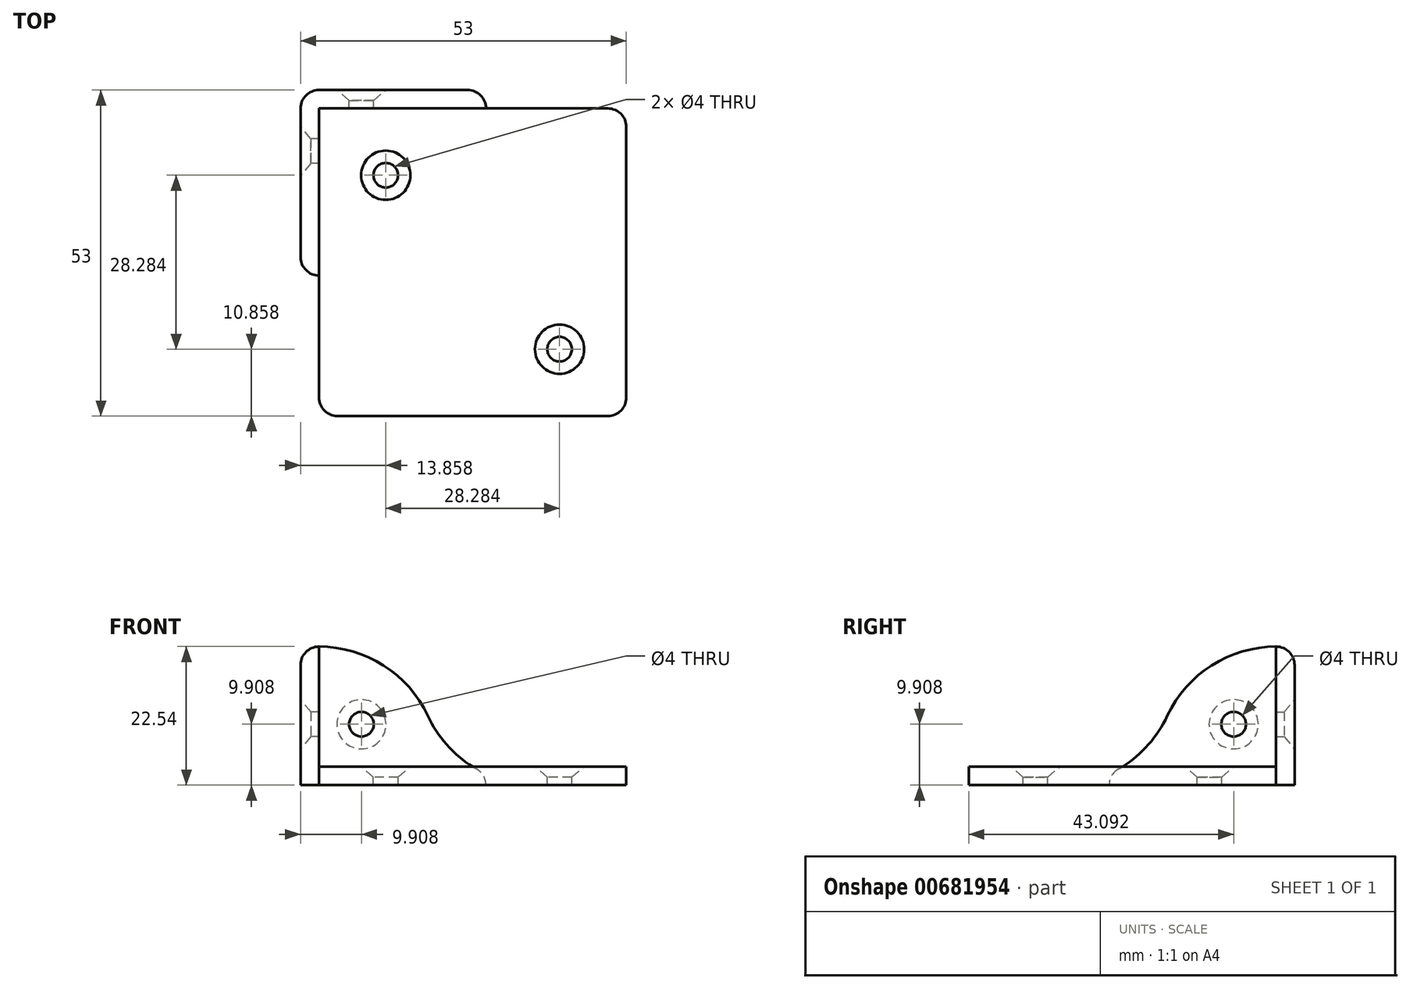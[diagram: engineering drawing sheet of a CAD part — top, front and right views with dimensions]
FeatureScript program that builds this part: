
annotation { "Feature Type Name" : "Feature", "Feature Type Description" : "" }
export const myFeature = defineFeature(function(context is Context, id is Id, definition is map)
    precondition{}
    {
        {
            var Q0;
            Q0=qCreatedBy(makeId("Top.planeOp"),FACE);
            var sketch = newSketch(context, id + "F0", { "sketchPlane" : qUnion([Q0])});
            skLineSegment(sketch, "E0.bottom", {"start": v(-25, 25) * mm, "end": v(25, 25) * mm});
            skLineSegment(sketch, "E0.top", {"start": v(-25, -25) * mm, "end": v(25, -25) * mm});
            skLineSegment(sketch, "E0.left", {"start": v(-25, 22) * mm, "end": v(-25, -25) * mm});
            skLineSegment(sketch, "E0.right", {"start": v(25, 25) * mm, "end": v(25, -25) * mm});
            skPoint(sketch, "E0.middle", {"position": v(0, 0) * mm});
            skLineSegment(sketch, "E1", {"start": v(-25, 25) * mm, "end": v(25, -25) * mm, "construction": true});
            skCircle(sketch, "E2", {"center": v(-14.14, 14.14) * mm, "radius": 2 * mm, "construction": true});
            skCircle(sketch, "E3", {"center": v(14.14, -14.14) * mm, "radius": 2 * mm, "construction": true});
            skCircle(sketch, "E4", {"center": v(-14.14, 14.14) * mm, "radius": 4 * mm, "construction": true});
            skCircle(sketch, "E5", {"center": v(14.14, -14.14) * mm, "radius": 4 * mm, "construction": true});
            skLineSegment(sketch, "E6.left", {"start": v(-28, 28) * mm, "end": v(-28, 25) * mm});
            skLineSegment(sketch, "E7", {"start": v(-28, 25) * mm, "end": v(-25, 22) * mm});
            skLineSegment(sketch, "E8", {"start": v(-28, 28) * mm, "end": v(-25, 25) * mm});
            skSolve(sketch);
        }
        {
            var Q0;
            Q0=makeQuery(id+"F0.imprint","IMPRINT",FACE,{"disambiguationData":[TD([[makeQuery(id+"F0.imprint","IMPRINT",EDGE,{"derivedFrom":sQuery(id+"F0.wireOp",EDGE,"E0.bottom")}),-1.0]])]});
            var Q1;
            Q1=makeQuery(id+"F0.imprint","IMPRINT",FACE,{"disambiguationData":[TD([[makeQuery(id+"F0.imprint","IMPRINT",EDGE,{"derivedFrom":sQuery(id+"F0.wireOp",EDGE,"E6.bottom")}),-1.0]])]});
            extrude(context, id + "F1", {"entities" : qUnion([Q0, Q1]), "oppositeDirection" : true, "depth" : 3 * mm, "offsetDistance" : 25 * mm});
        }
        {
            var Q0;
            Q0=makeQuery(id+"F1.opExtrude","SWEPT_FACE",FACE,{"disambiguationData":[OSD([sQuery(id+"F0.wireOp",EDGE,"E6.left")])]});
            var sketch = newSketch(context, id + "F2", { "sketchPlane" : qUnion([Q0])});
            skCircle(sketch, "E9", {"center": v(-18.1, 6.9) * mm, "radius": 4 * mm, "construction": true});
            skCircle(sketch, "E10", {"center": v(-18.1, 6.9) * mm, "radius": 2 * mm, "construction": true});
            skLineSegment(sketch, "E11", {"start": v(-25, 0) * mm, "end": v(-18.1, 6.9) * mm, "construction": true});
            skArc(sketch, "E12", {"start": v(-7.3, 8.27) * mm, "mid": v(-3.99, 3.32) * mm, "end": v(0.66, -0.4) * mm});
            skLineSegment(sketch, "E13", {"start": v(-18.1, 6.9) * mm, "end": v(-11.18, 13.82) * mm, "construction": true});
            skLineSegment(sketch, "E14", {"start": v(-28, 19.54) * mm, "end": v(-28, -3) * mm});
            skLineSegment(sketch, "E15", {"start": v(-28, -3) * mm, "end": v(2.17, -3) * mm});
            skArc(sketch, "E16", {"start": v(-7.3, 8.27) * mm, "mid": v(-14.5, 16.48) * mm, "end": v(-25, 19.54) * mm});
            skArc(sketch, "E17", {"start": v(2.17, -3) * mm, "mid": v(1.76, -1.5) * mm, "end": v(0.66, -0.4) * mm});
            skLineSegment(sketch, "E18", {"start": v(-28, 19.54) * mm, "end": v(-25, 19.54) * mm});
            skSolve(sketch);
        }
        {
            var Q0;
            {var subQ3=sQuery(id+"F2.wireOp",EDGE,"E14");Q0=makeQuery(id+"F2.imprint","IMPRINT",FACE,{"disambiguationData":[TD([[makeQuery(id+"F2.imprint","IMPRINT",EDGE,{"derivedFrom":subQ3}),1.0]])]});}
            var Q1;
            {var subQ3=sQuery(id+"F2.wireOp",EDGE,"E17");Q1=makeQuery(id+"F2.imprint","IMPRINT",FACE,{"disambiguationData":[TD([[makeQuery(id+"F2.imprint","IMPRINT",EDGE,{"derivedFrom":subQ3}),1.0]])]});}
            extrude(context, id + "F3", {"entities" : qUnion([Q0, Q1]), "operationType" : NewBodyOperationType.ADD, "oppositeDirection" : true, "depth" : 3 * mm, "offsetDistance" : 25 * mm});
        }
        {
            var Q0;
            Q0=sQuery(id+"F0.wireOp",VERTEX,"E4.center");
            var Q1;
            Q1=sQuery(id+"F0.wireOp",VERTEX,"E5.center");
            var Q2;
            Q2=makeQuery(id+"F1.opExtrude","SWEPT_BODY",BODY,{"disambiguationData":[OSD([sQuery(id+"F0.wireOp",EDGE,"E0.bottom"),sQuery(id+"F0.wireOp",EDGE,"E0.top"),sQuery(id+"F0.wireOp",EDGE,"E0.left"),sQuery(id+"F0.wireOp",EDGE,"E0.right")])]});
            hole(context, id + "F4", {"style" : HoleStyle.C_SINK, "endStyle" : HoleEndStyle.THROUGH, "holeDiameter" : 4 * mm, "cSinkDiameter" : 8 * mm, "cSinkAngle" : 100 * degree, "majorDiameter" : 5 * mm, "isTappedThrough" : true, "tappedDepth" : 12 * mm, "tapClearance" : 3, "locations" : qUnion([Q0, Q1]), "scope" : qUnion([Q2])});
        }
        {
            var Q0;
            Q0=sQuery(id+"F2.wireOp",VERTEX,"E13.start");
            var Q1;
            Q1=makeQuery(id+"F1.opExtrude","SWEPT_BODY",BODY,{"disambiguationData":[OSD([sQuery(id+"F0.wireOp",EDGE,"E0.bottom"),sQuery(id+"F0.wireOp",EDGE,"E0.top"),sQuery(id+"F0.wireOp",EDGE,"E0.left"),sQuery(id+"F0.wireOp",EDGE,"E0.right"),sQuery(id+"F0.wireOp",EDGE,"E6.bottom"),sQuery(id+"F0.wireOp",EDGE,"E6.left"),sQuery(id+"F0.wireOp",EDGE,"E7"),sQuery(id+"F0.wireOp",EDGE,"unFV2F4c-Ip1l-St1S-5ZnQ-sBuzKCw6DhjQ")])]});
            hole(context, id + "F5", {"style" : HoleStyle.C_SINK, "endStyle" : HoleEndStyle.THROUGH, "holeDiameter" : 4 * mm, "cSinkDiameter" : 8 * mm, "cSinkAngle" : 100 * degree, "majorDiameter" : 5 * mm, "isTappedThrough" : true, "tappedDepth" : 12 * mm, "tapClearance" : 3, "locations" : qUnion([Q0]), "scope" : qUnion([Q1])});
        }
        {
            var Q0;
            Q0=makeQuery(id+"F1.opExtrude","SWEPT_BODY",BODY,{"disambiguationData":[OSD([sQuery(id+"F0.wireOp",EDGE,"E0.bottom"),sQuery(id+"F0.wireOp",EDGE,"E0.top"),sQuery(id+"F0.wireOp",EDGE,"E0.left"),sQuery(id+"F0.wireOp",EDGE,"E0.right"),sQuery(id+"F0.wireOp",EDGE,"E6.left"),sQuery(id+"F0.wireOp",EDGE,"E7"),sQuery(id+"F0.wireOp",EDGE,"E8")])]});
            var Q1;
            Q1=makeQuery(id+"F1.opExtrude","SWEPT_FACE",FACE,{"disambiguationData":[OSD([sQuery(id+"F0.wireOp",EDGE,"E8")])]});
            mirror(context, id + "F6", {"operationType" : NewBodyOperationType.ADD, "entities" : qUnion([Q0]), "mirrorPlane" : qUnion([Q1])});
        }
        {
            var Q0;
            Q0=makeQuery(id+"F3.opExtrude","CAP_EDGE",EDGE,{"disambiguationData":[OSD([sQuery(id+"F2.wireOp",EDGE,"E16")])],"isStart":true});
            var Q1;
            Q1=makeQuery(id+"F6.opPattern","COPY",EDGE,{"derivedFrom":makeQuery(id+"F3.opExtrude","CAP_EDGE",EDGE,{"disambiguationData":[OSD([sQuery(id+"F2.wireOp",EDGE,"E16")])],"isStart":true}),"instanceName":"1"});
            var Q2;
            {var subQ0=makeQuery(id+"F1.opExtrude","SWEPT_EDGE",EDGE,{"disambiguationData":[OSD([sQuery(id+"F0.wireOp",EDGE,"E6.left"),sQuery(id+"F0.wireOp",EDGE,"E8")])]});Q2=makeQuery(id+"F6.boolean.opBoolean","MERGE",EDGE,{"derivedFrom":[subQ0,makeQuery(id+"F3.opExtrude","CAP_EDGE",EDGE,{"disambiguationData":[OSD([sQuery(id+"F2.wireOp",EDGE,"E14")])],"isStart":true}),makeQuery(id+"F6.opPattern","COPY",EDGE,{"derivedFrom":subQ0,"instanceName":"1"})]});}
            var Q3;
            Q3=makeQuery(id+"F1.opExtrude","SWEPT_EDGE",EDGE,{"disambiguationData":[OSD([sQuery(id+"F0.wireOp",EDGE,"E0.top"),sQuery(id+"F0.wireOp",EDGE,"E0.left")])]});
            var Q4;
            Q4=makeQuery(id+"F1.opExtrude","SWEPT_EDGE",EDGE,{"disambiguationData":[OSD([sQuery(id+"F0.wireOp",EDGE,"E0.top"),sQuery(id+"F0.wireOp",EDGE,"E0.right")])]});
            var Q5;
            Q5=makeQuery(id+"F1.opExtrude","SWEPT_EDGE",EDGE,{"disambiguationData":[OSD([sQuery(id+"F0.wireOp",EDGE,"E0.bottom"),sQuery(id+"F0.wireOp",EDGE,"E0.right")])]});
            fillet(context, id + "F7", {"entities" : qUnion([Q0, Q1, Q2, Q3, Q4, Q5]), "radius" : 3 * mm, "tangentPropagation" : true, "allowEdgeOverflow" : false});
        }
    });
